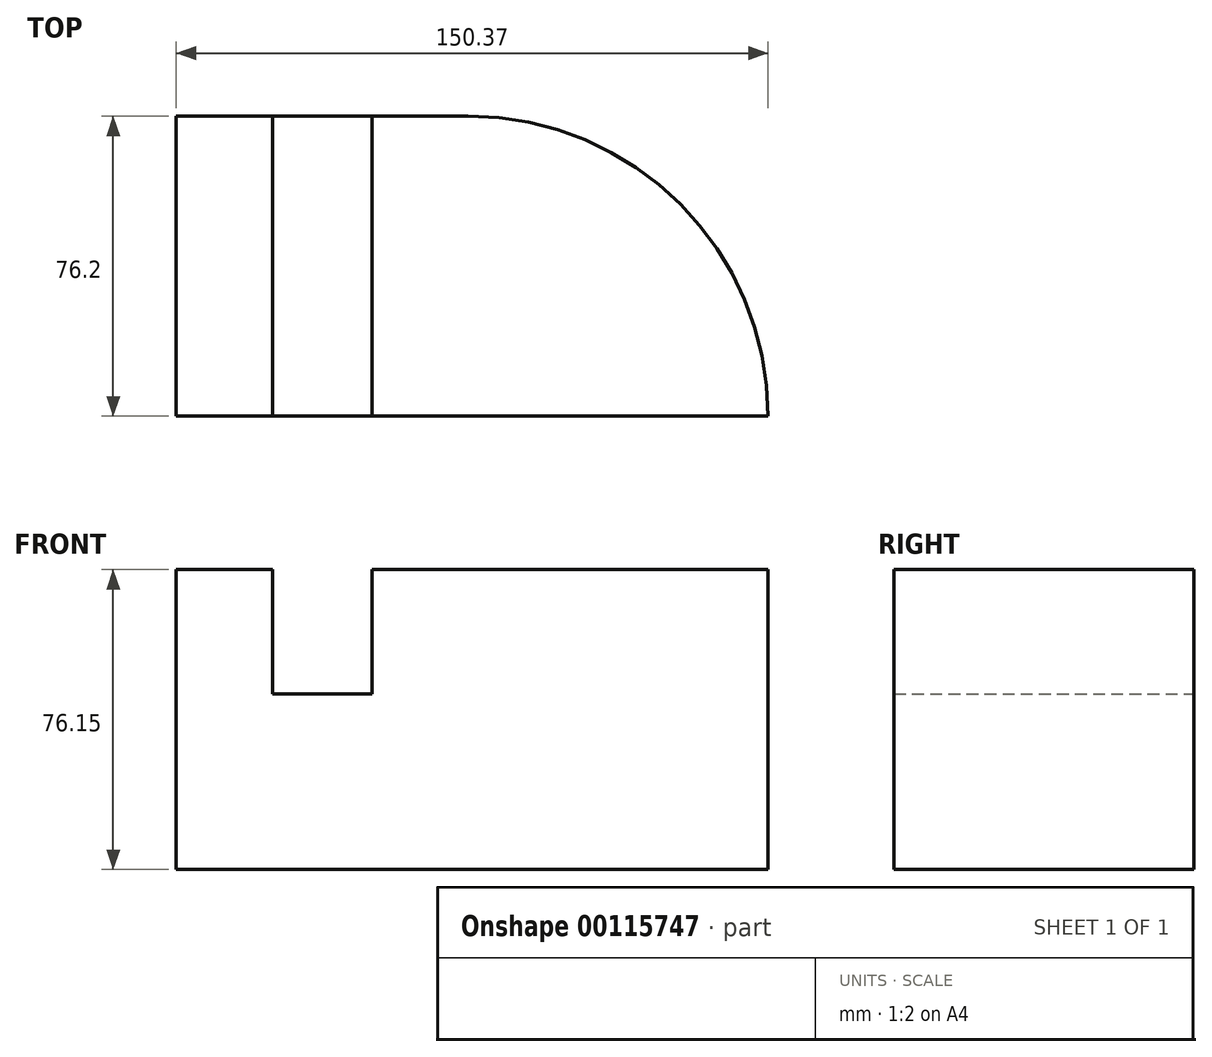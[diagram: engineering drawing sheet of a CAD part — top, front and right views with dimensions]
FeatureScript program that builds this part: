
annotation { "Feature Type Name" : "Feature", "Feature Type Description" : "" }
export const myFeature = defineFeature(function(context is Context, id is Id, definition is map)
    precondition{}
    {
        {
            var Q0;
            Q0=qCreatedBy(makeId("Front.planeOp"),FACE);
            var sketch = newSketch(context, id + "F0", { "sketchPlane" : qUnion([Q0])});
            skLineSegment(sketch, "E0.bottom", {"start": v(-40.59, 44.27) * mm, "end": v(-16.16, 44.27) * mm});
            skLineSegment(sketch, "E0.top", {"start": v(-40.59, -31.88) * mm, "end": v(33.58, -31.88) * mm});
            skLineSegment(sketch, "E0.left", {"start": v(-40.59, 44.27) * mm, "end": v(-40.59, -31.88) * mm});
            skLineSegment(sketch, "E0.right", {"start": v(33.58, 44.27) * mm, "end": v(33.58, -31.88) * mm});
            skLineSegment(sketch, "E1", {"start": v(-16.16, 44.27) * mm, "end": v(-16.16, 12.66) * mm});
            skLineSegment(sketch, "E2", {"start": v(-16.16, 12.66) * mm, "end": v(9.16, 12.66) * mm});
            skLineSegment(sketch, "E3", {"start": v(9.16, 12.66) * mm, "end": v(9.16, 44.27) * mm});
            skLineSegment(sketch, "E4.trimOffspring", {"start": v(9.16, 44.27) * mm, "end": v(33.58, 44.27) * mm});
            skSolve(sketch);
        }
        {
            var Q0;
            Q0=makeQuery(id+"F0.imprint","IMPRINT",FACE,{"disambiguationData":[TD([[makeQuery(id+"F0.imprint","IMPRINT",EDGE,{"derivedFrom":sQuery(id+"F0.wireOp",EDGE,"E0.bottom")}),-1.0]])]});
            extrude(context, id + "F1", {"entities" : qUnion([Q0]), "depth" : 76.2 * mm});
        }
        {
            var Q0;
            Q0=makeQuery(id+"F1.opExtrude","SWEPT_FACE",FACE,{"disambiguationData":[OSD([sQuery(id+"F0.wireOp",EDGE,"E0.right")])]});
            var Q1;
            Q1=makeQuery(id+"F1.opExtrude","CAP_EDGE",EDGE,{"disambiguationData":[OSD([sQuery(id+"F0.wireOp",EDGE,"E0.right")])],"isStart":false});
            revolve(context, id + "F2", {"operationType" : NewBodyOperationType.ADD, "entities" : qUnion([Q0]), "axis" : qUnion([Q1]), "revolveType" : RevolveType.ONE_DIRECTION, "angle" : 90 * degree});
        }
    });
